# Revit family: Furniture_Mirrors_Svedholm_Cyclops
name_source: partatom
category: Furniture
revit_build: Autodesk Revit 2018 (Build: 20190510_1515(x64)
units: mm (PartAtom-declared; Revit-internal decimal feet)

## family parameters
Cut with Voids When Loaded = No
Host = Face
OmniClass Number = 23.21.37.13.15
OmniClass Title = Mirrors
Room Calculation Point = No
Shared = No

## types (2) — shared parameters
BIMobject category = Mirrors
Default Elevation = 1219 mm
Description = Two one-eyed mirrors that can be combined in many ways. A mirror with powder coated steel frame and smoke coloured mirror glass. Other colours available upon request.
Design country = Sweden
Edition number = 1
IFC Classification = Object
Manufacturer = Svedholm
Manufacturer country = Sweden
Manufacturer name = Svedholm
Masterformat 2014 Code = 08 83 00
Masterformat 2014 Description = Mirrors
Material main = Mirror Glass
Material secondary = Powder coated steel
Mirror material = Svedholm - Glass - Mirror
Model = Cyclops
NBS Reference Code = 71-55
NBS Reference Description = Mirrors
OmniClass Code = 23-21 37 13 15
OmniClass Description = Mirrors
Product Guid = bd66927a-4bbd-4adf-98d3-cae38642a50b
Product SKU = Cyclops
Product data url = https://bimobject.com
Product family = Cyclops
Product group = Mirrors
Product name = Cyclops
Product url = https://www.svedholm.se
QR code = https://bimobject.com
URL = https://www.svedholm.se
Uniclass 1.4 Code = L8732
Uniclass 1.4 Description = Mirrors
Uniclass 2.0 Code = PR-71-55
Uniclass 2.0 Description = Mirrors
Uniclass 2015 Code = Pr_25_71_53
Uniclass 2015 Name = Mirrors

## type names
- ART - (124.600.001)
- ART - (124.600.002)
type visibility flags: 2 boolean params named "<type name>" — each type sets only its own to Yes (folded from table)

## geometry (parser evidence)
native form markers: Sweep x2
no freeform markers — native parametric forms only
